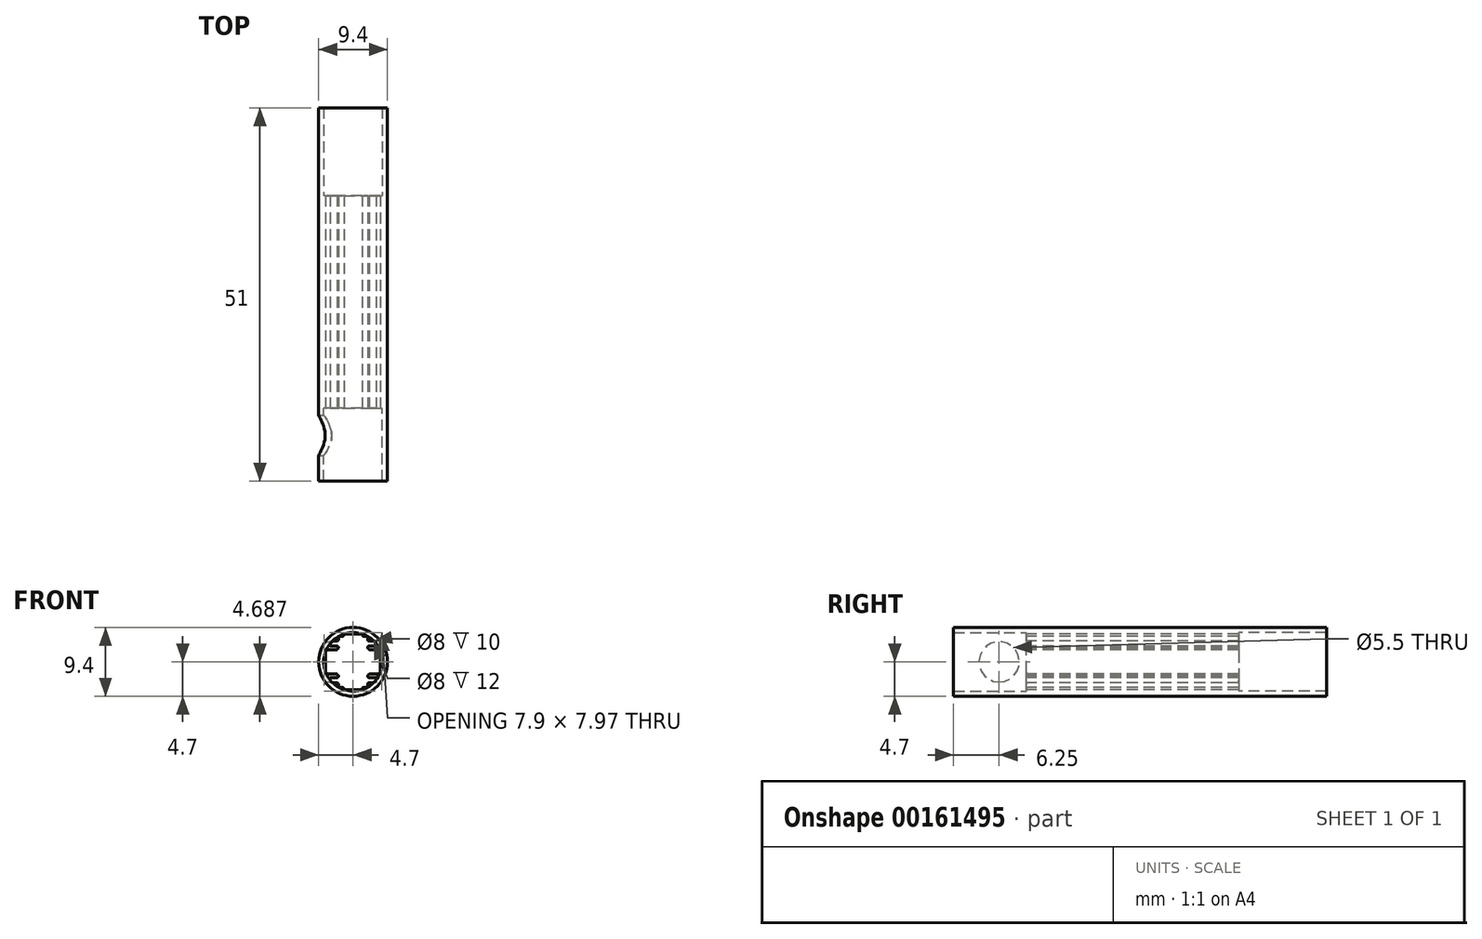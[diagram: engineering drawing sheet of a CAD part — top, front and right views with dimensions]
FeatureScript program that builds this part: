
annotation { "Feature Type Name" : "Feature", "Feature Type Description" : "" }
export const myFeature = defineFeature(function(context is Context, id is Id, definition is map)
    precondition{}
    {
        {
            assignVariable(context, id + "F0", {"name" : "Main_Length", "anyValue" : 51});
        }
        {
            assignVariable(context, id + "F1", {"name" : "Bore_Depth_F", "anyValue" : 10});
        }
        {
            assignVariable(context, id + "F2", {"name" : "Bore_Depth_R", "anyValue" : 12});
        }
        {
            var Q0;
            Q0=qCreatedBy(makeId("Front.planeOp"),FACE);
            var sketch = newSketch(context, id + "F3", { "sketchPlane" : qUnion([Q0])});
            skCircle(sketch, "E0", {"center": v(0, 0) * mm, "radius": 4.7 * mm});
            skSolve(sketch);
        }
        {
            var Q0;
            Q0=makeQuery(id+"F3.imprint","IMPRINT",FACE,{"disambiguationData":[TD([[makeQuery(id+"F3.imprint","IMPRINT",EDGE,{"derivedFrom":sQuery(id+"F3.wireOp",EDGE,"E0")}),1.0]])]});
            extrude(context, id + "F4", {"entities" : qUnion([Q0]), "depth" : (getVariable(context, 'Main_Length') - getVariable(context, 'Bore_Depth_F') - getVariable(context, 'Bore_Depth_R')) * mm});
        }
        {
            var Q0;
            Q0=makeQuery(id+"F4.opExtrude","CAP_FACE",FACE,{"disambiguationData":[OSD([sQuery(id+"F3.wireOp",EDGE,"E0")])],"isStart":false});
            var sketch = newSketch(context, id + "F5", { "sketchPlane" : qUnion([Q0])});
            skLineSegment(sketch, "E1", {"start": v(0, -3.8) * mm, "end": v(1.25, -3.8) * mm});
            skLineSegment(sketch, "E2", {"start": v(3.75, -1.65) * mm, "end": v(3.75, 0) * mm});
            skLineSegment(sketch, "E3", {"start": v(1.45, -3.5) * mm, "end": v(2, -3.5) * mm});
            skLineSegment(sketch, "E4", {"start": v(3.15, 2.15) * mm, "end": v(2.2, 2.15) * mm});
            skLineSegment(sketch, "E5", {"start": v(2, -1.95) * mm, "end": v(2, -1.89) * mm});
            skLineSegment(sketch, "E6", {"start": v(1.25, -3.8) * mm, "end": v(1.25, -3.7) * mm});
            skArc(sketch, "E7", {"start": v(2, -1.95) * mm, "mid": v(2.06, -2.1) * mm, "end": v(2.2, -2.15) * mm});
            skArc(sketch, "E8", {"start": v(1.45, -3.5) * mm, "mid": v(1.3, -3.56) * mm, "end": v(1.25, -3.7) * mm});
            skArc(sketch, "E9", {"start": v(2.2, 2.85) * mm, "mid": v(2.06, 2.9) * mm, "end": v(2, 3.05) * mm});
            skArc(sketch, "E10", {"start": v(2, 1.95) * mm, "mid": v(2.06, 2.1) * mm, "end": v(2.2, 2.15) * mm});
            skArc(sketch, "E11", {"start": v(2.2, -2.85) * mm, "mid": v(2.06, -2.9) * mm, "end": v(2, -3.05) * mm});
            skLineSegment(sketch, "E12", {"start": v(1.25, 3.8) * mm, "end": v(1.25, 3.7) * mm});
            skLineSegment(sketch, "E13", {"start": v(-3.75, -1.65) * mm, "end": v(-3.75, 0) * mm});
            skLineSegment(sketch, "E14", {"start": v(-3.15, -2.15) * mm, "end": v(-2.2, -2.15) * mm});
            skLineSegment(sketch, "E15", {"start": v(-3.15, -2.85) * mm, "end": v(-3.15, -2.15) * mm});
            skLineSegment(sketch, "E16", {"start": v(-2.2, -2.85) * mm, "end": v(-3.15, -2.85) * mm});
            skLineSegment(sketch, "E17", {"start": v(-2, -3.5) * mm, "end": v(-2, -3.05) * mm});
            skArc(sketch, "E18", {"start": v(-2.2, -2.85) * mm, "mid": v(-2.06, -2.9) * mm, "end": v(-2, -3.05) * mm});
            skLineSegment(sketch, "E19", {"start": v(-2, -1.95) * mm, "end": v(-2, -1.89) * mm});
            skLineSegment(sketch, "E20", {"start": v(-1.25, -3.8) * mm, "end": v(-1.25, -3.7) * mm});
            skArc(sketch, "E21", {"start": v(-1.45, 3.5) * mm, "mid": v(-1.3, 3.56) * mm, "end": v(-1.25, 3.7) * mm});
            skLineSegment(sketch, "E22", {"start": v(-3.15, 2.15) * mm, "end": v(-2.2, 2.15) * mm});
            skLineSegment(sketch, "E23", {"start": v(2.2, -2.85) * mm, "end": v(3.15, -2.85) * mm});
            skLineSegment(sketch, "E24", {"start": v(2.2, -1.65) * mm, "end": v(3.75, -1.65) * mm});
            skLineSegment(sketch, "E25", {"start": v(-2.2, 2.85) * mm, "end": v(-3.15, 2.85) * mm});
            skLineSegment(sketch, "E26", {"start": v(-1.45, 3.5) * mm, "end": v(-2, 3.5) * mm});
            skLineSegment(sketch, "E27", {"start": v(0, 3.8) * mm, "end": v(-1.25, 3.8) * mm});
            skLineSegment(sketch, "E28", {"start": v(3.15, -2.85) * mm, "end": v(3.15, -2.15) * mm});
            skLineSegment(sketch, "E29", {"start": v(-1.45, -3.5) * mm, "end": v(-2, -3.5) * mm});
            skLineSegment(sketch, "E30", {"start": v(-2, 3.5) * mm, "end": v(-2, 3.05) * mm});
            skArc(sketch, "E31", {"start": v(-1.45, -3.5) * mm, "mid": v(-1.3, -3.56) * mm, "end": v(-1.25, -3.7) * mm});
            skArc(sketch, "E32", {"start": v(-2, 1.95) * mm, "mid": v(-2.06, 2.1) * mm, "end": v(-2.2, 2.15) * mm});
            skArc(sketch, "E33", {"start": v(2, -1.89) * mm, "mid": v(2.1, -1.77) * mm, "end": v(2.2, -1.65) * mm});
            skLineSegment(sketch, "E34", {"start": v(2.2, 1.65) * mm, "end": v(3.75, 1.65) * mm});
            skLineSegment(sketch, "E35", {"start": v(3.15, 2.85) * mm, "end": v(3.15, 2.15) * mm});
            skLineSegment(sketch, "E36", {"start": v(2, -3.5) * mm, "end": v(2, -3.05) * mm});
            skLineSegment(sketch, "E37", {"start": v(-2.2, -1.65) * mm, "end": v(-3.75, -1.65) * mm});
            skLineSegment(sketch, "E38", {"start": v(-3.75, 1.65) * mm, "end": v(-3.75, 0) * mm});
            skLineSegment(sketch, "E39", {"start": v(0, -3.8) * mm, "end": v(-1.25, -3.8) * mm});
            skLineSegment(sketch, "E40", {"start": v(2, 1.95) * mm, "end": v(2, 1.89) * mm});
            skLineSegment(sketch, "E41", {"start": v(-3.15, 2.85) * mm, "end": v(-3.15, 2.15) * mm});
            skLineSegment(sketch, "E42", {"start": v(0, 3.8) * mm, "end": v(1.25, 3.8) * mm});
            skLineSegment(sketch, "E43", {"start": v(3.15, -2.15) * mm, "end": v(2.2, -2.15) * mm});
            skLineSegment(sketch, "E44", {"start": v(-2.2, 1.65) * mm, "end": v(-3.75, 1.65) * mm});
            skLineSegment(sketch, "E45", {"start": v(-1.25, 3.8) * mm, "end": v(-1.25, 3.7) * mm});
            skArc(sketch, "E46", {"start": v(-2, -1.95) * mm, "mid": v(-2.06, -2.1) * mm, "end": v(-2.2, -2.15) * mm});
            skArc(sketch, "E47", {"start": v(2.2, 1.65) * mm, "mid": v(2.1, 1.77) * mm, "end": v(2, 1.89) * mm});
            skArc(sketch, "E48", {"start": v(-2.2, 2.85) * mm, "mid": v(-2.06, 2.9) * mm, "end": v(-2, 3.05) * mm});
            skLineSegment(sketch, "E49", {"start": v(-2, 1.95) * mm, "end": v(-2, 1.89) * mm});
            skArc(sketch, "E50", {"start": v(1.45, 3.5) * mm, "mid": v(1.3, 3.56) * mm, "end": v(1.25, 3.7) * mm});
            skLineSegment(sketch, "E51", {"start": v(3.75, 1.65) * mm, "end": v(3.75, 0) * mm});
            skLineSegment(sketch, "E52", {"start": v(1.45, 3.5) * mm, "end": v(2, 3.5) * mm});
            skLineSegment(sketch, "E53", {"start": v(2.2, 2.85) * mm, "end": v(3.15, 2.85) * mm});
            skLineSegment(sketch, "E54", {"start": v(2, 3.5) * mm, "end": v(2, 3.05) * mm});
            skArc(sketch, "E55", {"start": v(-2.2, -1.65) * mm, "mid": v(-2.1, -1.77) * mm, "end": v(-2, -1.89) * mm});
            skArc(sketch, "E56", {"start": v(-2, 1.89) * mm, "mid": v(-2.1, 1.77) * mm, "end": v(-2.2, 1.65) * mm});
            skSolve(sketch);
        }
        {
            var Q0;
            Q0=makeQuery(id+"F4.opExtrude","CAP_FACE",FACE,{"disambiguationData":[OSD([sQuery(id+"F3.wireOp",EDGE,"E0")])],"isStart":false});
            var sketch = newSketch(context, id + "F6", { "sketchPlane" : qUnion([Q0])});
            skCircle(sketch, "E57.0", {"center": v(0, 0) * mm, "radius": 4.7 * mm});
            skCircle(sketch, "E58", {"center": v(0, 0) * mm, "radius": 4 * mm});
            skSolve(sketch);
        }
        {
            var Q0;
            Q0=makeQuery(id+"F4.opExtrude","CAP_FACE",FACE,{"disambiguationData":[OSD([sQuery(id+"F3.wireOp",EDGE,"E0")])],"isStart":true});
            var sketch = newSketch(context, id + "F7", { "sketchPlane" : qUnion([Q0])});
            skCircle(sketch, "E59.0", {"center": v(0, 0) * mm, "radius": 4.7 * mm});
            skCircle(sketch, "E60", {"center": v(0, 0) * mm, "radius": 4 * mm});
            skSolve(sketch);
        }
        {
            var Q0;
            Q0=makeQuery(id+"F5.imprint","IMPRINT",FACE,{"disambiguationData":[TD([[makeQuery(id+"F5.imprint","IMPRINT",EDGE,{"derivedFrom":sQuery(id+"F5.wireOp",EDGE,"E1")}),1.0]])]});
            extrude(context, id + "F8", {"entities" : qUnion([Q0]), "operationType" : NewBodyOperationType.REMOVE, "endBound" : BoundingType.UP_TO_NEXT, "oppositeDirection" : true, "depth" : 25 * mm});
        }
        {
            var Q0;
            Q0=makeQuery(id+"F6.imprint","IMPRINT",FACE,{"disambiguationData":[TD([[makeQuery(id+"F6.imprint","IMPRINT",EDGE,{"derivedFrom":sQuery(id+"F6.wireOp",EDGE,"E57.0")}),1.0]])]});
            extrude(context, id + "F9", {"entities" : qUnion([Q0]), "operationType" : NewBodyOperationType.ADD, "depth" : (getVariable(context, 'Bore_Depth_F')) * mm});
        }
        {
            var Q0;
            Q0=makeQuery(id+"F7.imprint","IMPRINT",FACE,{"disambiguationData":[TD([[makeQuery(id+"F7.imprint","IMPRINT",EDGE,{"derivedFrom":sQuery(id+"F7.wireOp",EDGE,"E59.0")}),-1.0]])]});
            extrude(context, id + "F10", {"entities" : qUnion([Q0]), "operationType" : NewBodyOperationType.ADD, "depth" : (getVariable(context, 'Bore_Depth_R')) * mm});
        }
        {
            var Q0;
            Q0=qCreatedBy(makeId("Right.planeOp"),FACE);
            var sketch = newSketch(context, id + "F11", { "sketchPlane" : qUnion([Q0])});
            skCircle(sketch, "E61", {"center": v(-32.75, 0) * mm, "radius": 2.75 * mm});
            skSolve(sketch);
        }
        {
            var Q0;
            Q0=makeQuery(id+"F11.imprint","IMPRINT",FACE,{"disambiguationData":[TD([[makeQuery(id+"F11.imprint","IMPRINT",EDGE,{"derivedFrom":sQuery(id+"F11.wireOp",EDGE,"E61")}),1.0]])]});
            extrude(context, id + "F12", {"entities" : qUnion([Q0]), "operationType" : NewBodyOperationType.REMOVE, "endBound" : BoundingType.THROUGH_ALL, "oppositeDirection" : true, "depth" : 25 * mm});
        }
    });
